# Revit family: protivipozarnae_stora_firetechnics_ei60_120_c_oracheniem_vodoi
name_source: partatom
category: Двери
revit_build: Autodesk Revit 2018 (Build: 20170223_1515(x64)
units: mm (PartAtom-declared; Revit-internal decimal feet)

## family parameters
Всегда вертикально = Да
Заголовок OmniClass = Doors
Номер OmniClass = 23.30.10.00
Общий = Нет
Основа = Стена
При загрузке вырезать с полостями = Нет
Точка расчета площади = Нет

## types (3) — shared parameters
ADSK_URL страницы изделия = https://www.fire-tec.ru
ADSK_Завод-изготовитель = Firetechnics
ADSK_Размер_Высота = 3000 мм
ADSK_Размер_Ширина = 3000 мм
URL = https://www.fire-tec.ru
Аналитическая конструкция = <Нет>
Высота = 3000 мм
Высота короба = 150 мм
Высота, макс. = 6.5м
Замыкание стены = По основе
Изготовитель = Firetechnics
Комментарии к типоразмеру = Без орошения водой
Материал_Короб = Сталь_оцинкованная_листовая_2мм_Firetechnics
Материал_Направляющие = Сталь_оцинкованная_листовая Firetechnics
Материал_Полотно = Firetex™ 1100
Полотно = 1 мм
Полотно_Размещение = 30 мм
Скорость опускания шторы = 0,15м/c
Функция = Внутренние слои
Ширина = 3000 мм
Ширина направляющей = 80 мм
Ширина, макс. = 5м
высота направляющей = 60 мм
ширина верхней балки = 150 мм
ширина полотна = 3020 мм

## per-type parameters (varying)
| type | ADSK_Наименование | ADSK_Предел огнестойкости | Материал_Лаза | Огнестойкость |
| EI60 (с орошением водой) | Противопожарная штора FireTechnics EI60 (с орошением водой) | EI60 | Материал двери-лазейки | EI60 |
| EI120 (с орошением водой) | Противопожарная штора FireTechnics EI120 (с орошением водой) | EI120 | <По категории> | EI120 |
| EI180 (с орошением водой) | Противопожарная штора FireTechnics EI180 (с орошением водой) | EI180 | Материал двери-лазейки | EI180 |

## geometry (parser evidence)
native form markers: Blend x2
no freeform markers — native parametric forms only
